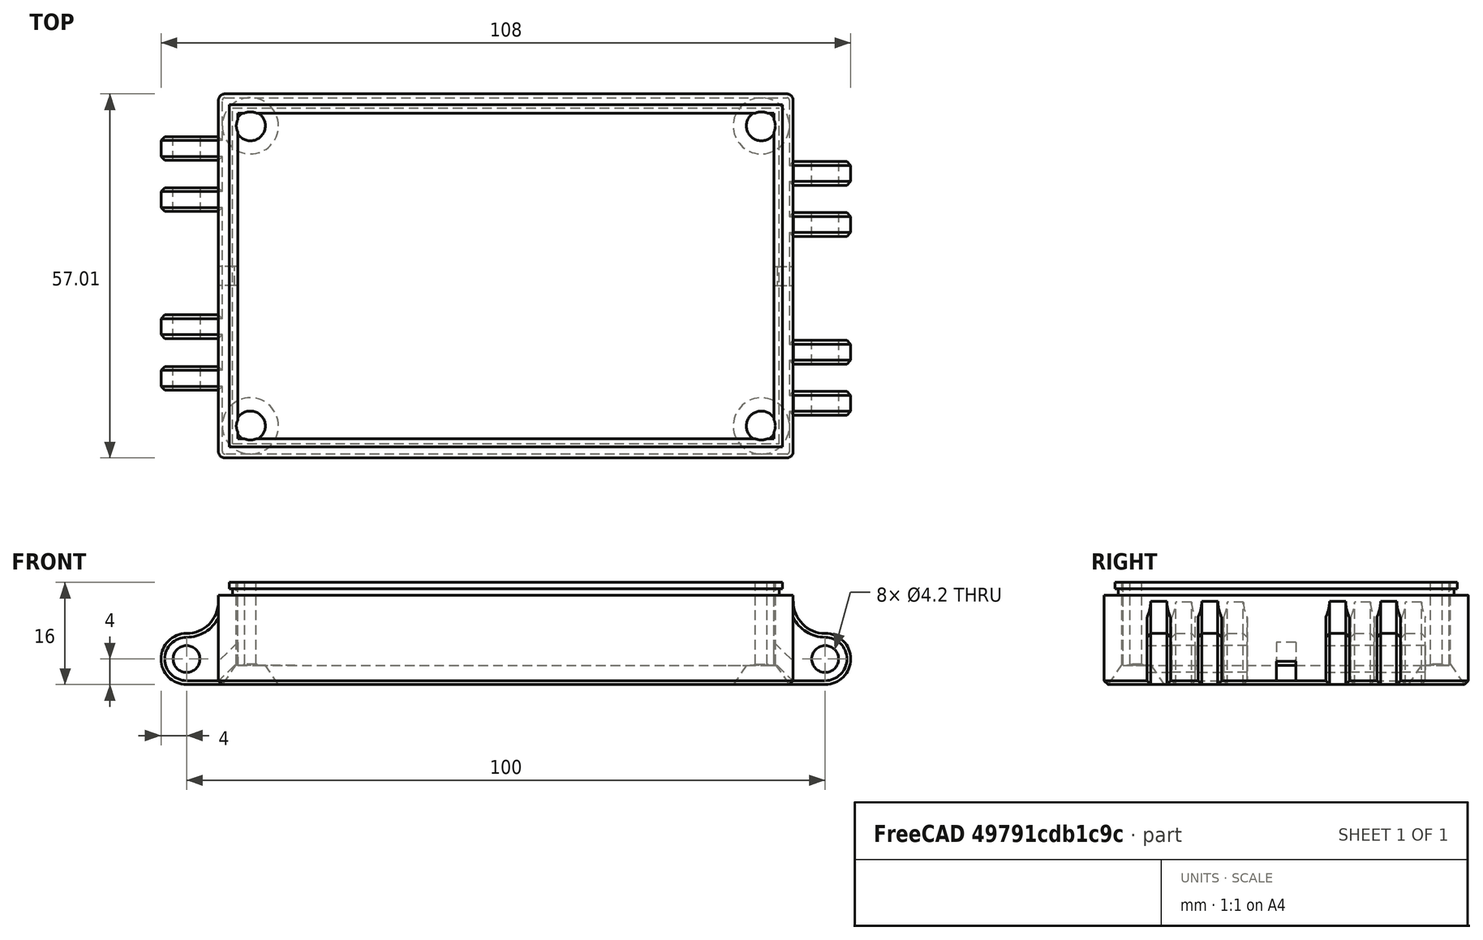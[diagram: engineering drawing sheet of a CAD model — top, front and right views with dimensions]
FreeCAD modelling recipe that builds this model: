
FCSTD DOCUMENT  (FreeCAD 0.16R)
Label: BoxBottom
License: All rights reserved
LicenseURL: http://en.wikipedia.org/wiki/All_rights_reserved
objects: Part::Chamfer×17, Part::Box×13, Part::MultiFuse×11, Sketcher::SketchObject×9, PartDesign::Pad×9, Part::Cut×5, Part::Cylinder×4, Part::Cone×4, Mesh::Feature×1
note: 81 computed .brp shape members not serialized (recipe doc carries the construction recipe); baked Part::Feature solids carry a one-line shape summary decoded from their .brp

FEATURE [Sketcher::SketchObject] Sketch002
  sketch-geometry (8):
    g0: LineSegment StartX=16.0115 StartY=-28 StartZ=0 EndX=-72 EndY=-28 EndZ=0
    g1: LineSegment StartX=-73.0008 StartY=-26.9992 StartZ=0 EndX=-73.0008 EndY=28.0015 EndZ=0
    g2: LineSegment StartX=-71.9972 StartY=29.005 StartZ=0 EndX=15.9984 EndY=29.005 EndZ=0
    g3: LineSegment StartX=16.9833 StartY=28.0201 StartZ=0 EndX=16.9833 EndY=-27.0282 EndZ=0
    g4: ArcOfCircle CenterX=16.0115 CenterY=-27.0282 CenterZ=0 NormalX=0 NormalY=0 NormalZ=1 Radius=0.97176 StartAngle=4.71239 EndAngle=6.28319
    g5: ArcOfCircle CenterX=-72 CenterY=-26.9992 CenterZ=0 NormalX=0 NormalY=0 NormalZ=1 Radius=1.00077 StartAngle=3.14159 EndAngle=4.71239
    g6: ArcOfCircle CenterX=-71.9972 CenterY=28.0015 CenterZ=0 NormalX=0 NormalY=0 NormalZ=1 Radius=1.00354 StartAngle=1.5708 EndAngle=3.14159
    g7: ArcOfCircle CenterX=15.9984 CenterY=28.0201 CenterZ=0 NormalX=0 NormalY=0 NormalZ=1 Radius=0.984903 StartAngle=0 EndAngle=1.5708
  constraints (12):
    c: Horizontal(g0)
    c: Horizontal(g2)
    c: Vertical(g1)
    c: Vertical(g3)
    c: Tangent(g3,g4) = 1.5708
    c: Tangent(g0,g4) = 1.5708
    c: Tangent(g1,g5) = 1.5708
    c: Tangent(g0,g5) = 1.5708
    c: Tangent(g1,g6) = 1.5708
    c: Tangent(g2,g6) = 1.5708
    c: Tangent(g2,g7) = 1.5708
    c: Tangent(g3,g7) = 1.5708
FEATURE [PartDesign::Pad] Pad013
  Length = 16
  Length2 = 100
  Sketch = -> Sketch002
  Type = 0
FEATURE [Part::Box] Box010  label="Würfel010"
  Height = 25
  Length = 84
  Placement = pos=(-70,-25,3) rot=(0,0,1;0rad)
  Width = 51
FEATURE [Part::Cut] Cut011
  Base = -> Pad013
  Tool = -> Box010
FEATURE [Part::Box] Box  label="Rand002"
  Height = 2
  Length = 90
  Placement = pos=(-73,27.3,14) rot=(0,0,1;0rad)
  Width = 2
FEATURE [Part::Box] Box011  label="Rand001"
  Height = 2
  Length = 90
  Placement = pos=(-73,-28.3,14) rot=(0,0,1;0rad)
  Width = 2
FEATURE [Part::Box] Box012  label="Rand003"
  Height = 2
  Length = 2
  Placement = pos=(-73.3,-28,14) rot=(0,0,1;0rad)
  Width = 57
FEATURE [Part::Box] Box013  label="Rand004"
  Height = 2
  Length = 2
  Placement = pos=(15.3,-28,14) rot=(0,0,1;0rad)
  Width = 57
FEATURE [Part::MultiFuse] Fusion  label="RandFraesung"
  Shapes = -> [Box013,Box012,Box011,Box]
FEATURE [Part::Cut] Cut
  Base = -> Cut011
  Tool = -> Fusion
FEATURE [Part::Box] Box014  label="Rand005"
  Height = 1
  Length = 90
  Placement = pos=(-74,26.8,14) rot=(0,0,1;0rad)
  Width = 1
FEATURE [Part::Box] Box015  label="Rand006"
  Height = 1
  Length = 90
  Placement = pos=(-74,-26.8,14) rot=(0,0,1;0rad)
  Width = 1
FEATURE [Part::Box] Box016  label="Rand007"
  Height = 1
  Length = 1
  Placement = pos=(-71.8,-28,14) rot=(0,0,1;0rad)
  Width = 57
FEATURE [Part::Box] Box017  label="Rand008"
  Height = 1
  Length = 1
  Placement = pos=(14.8,-28,14) rot=(0,0,1;0rad)
  Width = 57
FEATURE [Part::MultiFuse] Fusion001  label="NutFraesung"
  Shapes = -> [Box017,Box014,Box015,Box016]
FEATURE [Part::Cut] Cut012
  Base = -> Cut
  Tool = -> Fusion001
FEATURE [Part::Chamfer] Chamfer
  Base = -> Cut012
  Edges = 1 edges r=0.6: [Edge1]
FEATURE [Part::Box] Box018  label="Kabeltunnel"
  Height = 2.2
  Length = 10
  Placement = pos=(12,-1,5.5) rot=(0,1,0;0.785398rad)
  Width = 3
FEATURE [Sketcher::SketchObject] MirroredSketch004
  Placement = pos=(0,0,0) rot=(1,0,0;1.5708rad)
  sketch-geometry (7):
    g0: ArcOfCircle CenterX=0 CenterY=0 CenterZ=0 NormalX=0 NormalY=0 NormalZ=1 Radius=4 StartAngle=4.71239 EndAngle=7.85398
    g1: Circle CenterX=0 CenterY=0 CenterZ=0 NormalX=0 NormalY=0 NormalZ=1 Radius=2.1
    g2: LineSegment StartX=-6 StartY=9 StartZ=0 EndX=-6 EndY=-4 EndZ=0
    g3: LineSegment StartX=-6 StartY=-4 StartZ=0 EndX=0 EndY=-4 EndZ=0
    g4: LineSegment StartX=-5.47498 StartY=9 StartZ=0 EndX=-5 EndY=9 EndZ=0
    g5: ArcOfCircle CenterX=0 CenterY=9 CenterZ=0 NormalX=0 NormalY=0 NormalZ=1 Radius=5 StartAngle=3.14159 EndAngle=4.71239
    g6: LineSegment StartX=-6 StartY=9 StartZ=0 EndX=-5.47498 EndY=9 EndZ=0
  constraints (7):
    c: Coincident(g2,g3)
    c: Horizontal(g3)
    c: Vertical(g2)
    c: Coincident(g0,g3)
    c: Coincident(g5,g0)
    c: Coincident(g6,g4)
    c: Horizontal(g6)
FEATURE [PartDesign::Pad] Pad017  label="Lasche2Rechts004"
  Length = 3.7
  Length2 = 100
  Placement = pos=(0,0,0) rot=(1,0,0;1.5708rad)
  Sketch = -> MirroredSketch004
  Type = 0
FEATURE [Part::Chamfer] Chamfer009
  Base = -> Pad017
  Edges = 3 edges r=0.6: [Edge7,Edge10,Edge13]
FEATURE [Part::Chamfer] Chamfer010  label="Lasche2Rechts005"
  Base = -> Chamfer009
  Edges = 3 edges r=0.6: [Edge7,Edge11,Edge12]
  Placement = pos=(22,-17.6,4) rot=(0,0,1;0rad)
FEATURE [Sketcher::SketchObject] MirroredSketch005
  Placement = pos=(0,0,0) rot=(1,0,0;1.5708rad)
  sketch-geometry (7):
    g0: ArcOfCircle CenterX=0 CenterY=0 CenterZ=0 NormalX=0 NormalY=0 NormalZ=1 Radius=4 StartAngle=4.71239 EndAngle=7.85398
    g1: Circle CenterX=0 CenterY=0 CenterZ=0 NormalX=0 NormalY=0 NormalZ=1 Radius=2.1
    g2: LineSegment StartX=-6 StartY=9 StartZ=0 EndX=-6 EndY=-4 EndZ=0
    g3: LineSegment StartX=-6 StartY=-4 StartZ=0 EndX=0 EndY=-4 EndZ=0
    g4: LineSegment StartX=-5.47498 StartY=9 StartZ=0 EndX=-5 EndY=9 EndZ=0
    g5: ArcOfCircle CenterX=0 CenterY=9 CenterZ=0 NormalX=0 NormalY=0 NormalZ=1 Radius=5 StartAngle=3.14159 EndAngle=4.71239
    g6: LineSegment StartX=-6 StartY=9 StartZ=0 EndX=-5.47498 EndY=9 EndZ=0
  constraints (7):
    c: Coincident(g2,g3)
    c: Horizontal(g3)
    c: Vertical(g2)
    c: Coincident(g0,g3)
    c: Coincident(g5,g0)
    c: Coincident(g6,g4)
    c: Horizontal(g6)
FEATURE [PartDesign::Pad] Pad018  label="Lasche2Rechts006"
  Length = 3.7
  Length2 = 100
  Placement = pos=(0,0,0) rot=(1,0,0;1.5708rad)
  Sketch = -> MirroredSketch005
  Type = 0
FEATURE [Part::Chamfer] Chamfer011
  Base = -> Pad018
  Edges = 3 edges r=0.6: [Edge7,Edge10,Edge13]
FEATURE [Part::Chamfer] Chamfer012  label="Lasche2Rechts007"
  Base = -> Chamfer011
  Edges = 3 edges r=0.6: [Edge7,Edge11,Edge12]
  Placement = pos=(22,-9.6,4) rot=(0,0,1;0rad)
FEATURE [Sketcher::SketchObject] MirroredSketch006
  Placement = pos=(0,0,0) rot=(1,0,0;1.5708rad)
  sketch-geometry (7):
    g0: ArcOfCircle CenterX=0 CenterY=0 CenterZ=0 NormalX=0 NormalY=0 NormalZ=1 Radius=4 StartAngle=4.71239 EndAngle=7.85398
    g1: Circle CenterX=0 CenterY=0 CenterZ=0 NormalX=0 NormalY=0 NormalZ=1 Radius=2.1
    g2: LineSegment StartX=-6 StartY=9 StartZ=0 EndX=-6 EndY=-4 EndZ=0
    g3: LineSegment StartX=-6 StartY=-4 StartZ=0 EndX=0 EndY=-4 EndZ=0
    g4: LineSegment StartX=-5.47498 StartY=9 StartZ=0 EndX=-5 EndY=9 EndZ=0
    g5: ArcOfCircle CenterX=0 CenterY=9 CenterZ=0 NormalX=0 NormalY=0 NormalZ=1 Radius=5 StartAngle=3.14159 EndAngle=4.71239
    g6: LineSegment StartX=-6 StartY=9 StartZ=0 EndX=-5.47498 EndY=9 EndZ=0
  constraints (7):
    c: Coincident(g2,g3)
    c: Horizontal(g3)
    c: Vertical(g2)
    c: Coincident(g0,g3)
    c: Coincident(g5,g0)
    c: Coincident(g6,g4)
    c: Horizontal(g6)
FEATURE [PartDesign::Pad] Pad019  label="Lasche2Rechts008"
  Length = 3.7
  Length2 = 100
  Placement = pos=(0,0,0) rot=(1,0,0;1.5708rad)
  Sketch = -> MirroredSketch006
  Type = 0
FEATURE [Part::Chamfer] Chamfer013
  Base = -> Pad019
  Edges = 3 edges r=0.6: [Edge7,Edge10,Edge13]
FEATURE [Part::Chamfer] Chamfer014  label="Lasche2Rechts009"
  Base = -> Chamfer013
  Edges = 3 edges r=0.6: [Edge7,Edge11,Edge12]
  Placement = pos=(22,10.4,4) rot=(0,0,1;0rad)
FEATURE [Sketcher::SketchObject] MirroredSketch007
  Placement = pos=(0,0,0) rot=(1,0,0;1.5708rad)
  sketch-geometry (7):
    g0: ArcOfCircle CenterX=0 CenterY=0 CenterZ=0 NormalX=0 NormalY=0 NormalZ=1 Radius=4 StartAngle=4.71239 EndAngle=7.85398
    g1: Circle CenterX=0 CenterY=0 CenterZ=0 NormalX=0 NormalY=0 NormalZ=1 Radius=2.1
    g2: LineSegment StartX=-6 StartY=9 StartZ=0 EndX=-6 EndY=-4 EndZ=0
    g3: LineSegment StartX=-6 StartY=-4 StartZ=0 EndX=0 EndY=-4 EndZ=0
    g4: LineSegment StartX=-5.47498 StartY=9 StartZ=0 EndX=-5 EndY=9 EndZ=0
    g5: ArcOfCircle CenterX=0 CenterY=9 CenterZ=0 NormalX=0 NormalY=0 NormalZ=1 Radius=5 StartAngle=3.14159 EndAngle=4.71239
    g6: LineSegment StartX=-6 StartY=9 StartZ=0 EndX=-5.47498 EndY=9 EndZ=0
  constraints (7):
    c: Coincident(g2,g3)
    c: Horizontal(g3)
    c: Vertical(g2)
    c: Coincident(g0,g3)
    c: Coincident(g5,g0)
    c: Coincident(g6,g4)
    c: Horizontal(g6)
FEATURE [PartDesign::Pad] Pad020  label="Lasche2Rechts010"
  Length = 3.7
  Length2 = 100
  Placement = pos=(0,0,0) rot=(1,0,0;1.5708rad)
  Sketch = -> MirroredSketch007
  Type = 0
FEATURE [Part::Chamfer] Chamfer015
  Base = -> Pad020
  Edges = 3 edges r=0.6: [Edge7,Edge10,Edge13]
FEATURE [Part::Chamfer] Chamfer016  label="Lasche2Rechts011"
  Base = -> Chamfer015
  Edges = 3 edges r=0.6: [Edge7,Edge11,Edge12]
  Placement = pos=(22,18.4,4) rot=(0,0,1;0rad)
FEATURE [Part::Cylinder] Cylinder005  label="Zylinder"
  Angle = 360
  Height = 16
  Placement = pos=(12,-23,-1) rot=(0,0,1;0rad)
  Radius = 2.2
FEATURE [Part::Cone] Cone  label="Kegel"
  Angle = 360
  Height = 3.2
  Placement = pos=(12,-23,-1) rot=(0,0,1;0rad)
  Radius1 = 4.4
  Radius2 = 2.2
FEATURE [Part::MultiFuse] Fusion002  label="Bohrung001"
  Placement = pos=(0,0,1) rot=(0,0,1;0rad)
  Shapes = -> [Cylinder005,Cone]
FEATURE [Part::Cylinder] Cylinder006  label="Zylinder003"
  Angle = 360
  Height = 16
  Placement = pos=(12,-23,-1) rot=(0,0,1;0rad)
  Radius = 2.2
FEATURE [Part::Cone] Cone001  label="Kegel001"
  Angle = 360
  Height = 3.2
  Placement = pos=(12,-23,-1) rot=(0,0,1;0rad)
  Radius1 = 4.4
  Radius2 = 2.2
FEATURE [Part::MultiFuse] Fusion003  label="Bohrung002"
  Placement = pos=(0,47,1) rot=(0,0,1;0rad)
  Shapes = -> [Cylinder006,Cone001]
FEATURE [Part::Cylinder] Cylinder007  label="Zylinder004"
  Angle = 360
  Height = 16
  Placement = pos=(12,-23,-1) rot=(0,0,1;0rad)
  Radius = 2.2
FEATURE [Part::Cone] Cone002  label="Kegel002"
  Angle = 360
  Height = 3.2
  Placement = pos=(12,-23,-1) rot=(0,0,1;0rad)
  Radius1 = 4.4
  Radius2 = 2.2
FEATURE [Part::MultiFuse] Fusion004  label="Bohrung003"
  Placement = pos=(-80,0,1) rot=(0,0,1;0rad)
  Shapes = -> [Cylinder007,Cone002]
FEATURE [Part::Cylinder] Cylinder008  label="Zylinder005"
  Angle = 360
  Height = 16
  Placement = pos=(12,-23,-1) rot=(0,0,1;0rad)
  Radius = 2.2
FEATURE [Part::Cone] Cone003  label="Kegel003"
  Angle = 360
  Height = 3.2
  Placement = pos=(12,-23,-1) rot=(0,0,1;0rad)
  Radius1 = 4.4
  Radius2 = 2.2
FEATURE [Part::MultiFuse] Fusion005  label="Bohrung004"
  Placement = pos=(-80,47,1) rot=(0,0,1;0rad)
  Shapes = -> [Cylinder008,Cone003]
FEATURE [Part::MultiFuse] Fusion006  label="Bohrungen"
  Shapes = -> [Fusion003,Fusion002,Fusion004,Fusion005]
FEATURE [Part::Box] Box019  label="KabelTunnelGlatt"
  Height = 1
  Length = 10
  Placement = pos=(5,-1,3) rot=(0,0,1;0rad)
  Width = 3
FEATURE [Part::MultiFuse] Fusion007  label="Tunnel1"
  Shapes = -> [Box018,Box019]
FEATURE [Part::Box] Box020  label="Kabeltunnel001"
  Height = 2.2
  Length = 10
  Placement = pos=(12,-1,5.5) rot=(0,1,0;0.785398rad)
  Width = 3
FEATURE [Part::Box] Box021  label="KabelTunnelGlatt001"
  Height = 1
  Length = 10
  Placement = pos=(5,-1,3) rot=(0,0,1;0rad)
  Width = 3
FEATURE [Part::MultiFuse] Fusion008  label="Tunnel2"
  Placement = pos=(-56,1,0) rot=(0,0,1;3.14159rad)
  Shapes = -> [Box020,Box021]
FEATURE [Part::MultiFuse] Fusion009
  Shapes = -> [Fusion008,Fusion007]
FEATURE [Part::Cut] Cut013
  Base = -> Chamfer
  Tool = -> Fusion009
FEATURE [Sketcher::SketchObject] MirroredSketch008
  Placement = pos=(0,0,0) rot=(1,0,0;1.5708rad)
  sketch-geometry (7):
    g0: ArcOfCircle CenterX=0 CenterY=0 CenterZ=0 NormalX=0 NormalY=0 NormalZ=1 Radius=4 StartAngle=4.71239 EndAngle=7.85398
    g1: Circle CenterX=0 CenterY=0 CenterZ=0 NormalX=0 NormalY=0 NormalZ=1 Radius=2.1
    g2: LineSegment StartX=-6 StartY=9 StartZ=0 EndX=-6 EndY=-4 EndZ=0
    g3: LineSegment StartX=-6 StartY=-4 StartZ=0 EndX=0 EndY=-4 EndZ=0
    g4: LineSegment StartX=-5.47498 StartY=9 StartZ=0 EndX=-5 EndY=9 EndZ=0
    g5: ArcOfCircle CenterX=0 CenterY=9 CenterZ=0 NormalX=0 NormalY=0 NormalZ=1 Radius=5 StartAngle=3.14159 EndAngle=4.71239
    g6: LineSegment StartX=-6 StartY=9 StartZ=0 EndX=-5.47498 EndY=9 EndZ=0
  constraints (7):
    c: Coincident(g2,g3)
    c: Horizontal(g3)
    c: Vertical(g2)
    c: Coincident(g0,g3)
    c: Coincident(g5,g0)
    c: Coincident(g6,g4)
    c: Horizontal(g6)
FEATURE [PartDesign::Pad] Pad021  label="Lasche2Rechts012"
  Length = 3.7
  Length2 = 100
  Placement = pos=(0,0,0) rot=(1,0,0;1.5708rad)
  Sketch = -> MirroredSketch008
  Type = 0
FEATURE [Part::Chamfer] Chamfer017
  Base = -> Pad021
  Edges = 3 edges r=0.6: [Edge7,Edge10,Edge13]
FEATURE [Part::Chamfer] Chamfer018  label="Lasche2Rechts013"
  Base = -> Chamfer017
  Edges = 3 edges r=0.6: [Edge7,Edge11,Edge12]
  Placement = pos=(-78,18.6,4) rot=(0,0,1;3.14159rad)
FEATURE [Sketcher::SketchObject] MirroredSketch009
  Placement = pos=(0,0,0) rot=(1,0,0;1.5708rad)
  sketch-geometry (7):
    g0: ArcOfCircle CenterX=0 CenterY=0 CenterZ=0 NormalX=0 NormalY=0 NormalZ=1 Radius=4 StartAngle=4.71239 EndAngle=7.85398
    g1: Circle CenterX=0 CenterY=0 CenterZ=0 NormalX=0 NormalY=0 NormalZ=1 Radius=2.1
    g2: LineSegment StartX=-6 StartY=9 StartZ=0 EndX=-6 EndY=-4 EndZ=0
    g3: LineSegment StartX=-6 StartY=-4 StartZ=0 EndX=0 EndY=-4 EndZ=0
    g4: LineSegment StartX=-5.47498 StartY=9 StartZ=0 EndX=-5 EndY=9 EndZ=0
    g5: ArcOfCircle CenterX=0 CenterY=9 CenterZ=0 NormalX=0 NormalY=0 NormalZ=1 Radius=5 StartAngle=3.14159 EndAngle=4.71239
    g6: LineSegment StartX=-6 StartY=9 StartZ=0 EndX=-5.47498 EndY=9 EndZ=0
  constraints (7):
    c: Coincident(g2,g3)
    c: Horizontal(g3)
    c: Vertical(g2)
    c: Coincident(g0,g3)
    c: Coincident(g5,g0)
    c: Coincident(g6,g4)
    c: Horizontal(g6)
FEATURE [PartDesign::Pad] Pad022  label="Lasche2Rechts014"
  Length = 3.7
  Length2 = 100
  Placement = pos=(0,0,0) rot=(1,0,0;1.5708rad)
  Sketch = -> MirroredSketch009
  Type = 0
FEATURE [Part::Chamfer] Chamfer019
  Base = -> Pad022
  Edges = 3 edges r=0.6: [Edge7,Edge10,Edge13]
FEATURE [Part::Chamfer] Chamfer020  label="Lasche2Rechts015"
  Base = -> Chamfer019
  Edges = 3 edges r=0.6: [Edge7,Edge11,Edge12]
  Placement = pos=(-78,10.6,4) rot=(0,0,1;3.14159rad)
FEATURE [Sketcher::SketchObject] MirroredSketch010
  Placement = pos=(0,0,0) rot=(1,0,0;1.5708rad)
  sketch-geometry (7):
    g0: ArcOfCircle CenterX=0 CenterY=0 CenterZ=0 NormalX=0 NormalY=0 NormalZ=1 Radius=4 StartAngle=4.71239 EndAngle=7.85398
    g1: Circle CenterX=0 CenterY=0 CenterZ=0 NormalX=0 NormalY=0 NormalZ=1 Radius=2.1
    g2: LineSegment StartX=-6 StartY=9 StartZ=0 EndX=-6 EndY=-4 EndZ=0
    g3: LineSegment StartX=-6 StartY=-4 StartZ=0 EndX=0 EndY=-4 EndZ=0
    g4: LineSegment StartX=-5.47498 StartY=9 StartZ=0 EndX=-5 EndY=9 EndZ=0
    g5: ArcOfCircle CenterX=0 CenterY=9 CenterZ=0 NormalX=0 NormalY=0 NormalZ=1 Radius=5 StartAngle=3.14159 EndAngle=4.71239
    g6: LineSegment StartX=-6 StartY=9 StartZ=0 EndX=-5.47498 EndY=9 EndZ=0
  constraints (7):
    c: Coincident(g2,g3)
    c: Horizontal(g3)
    c: Vertical(g2)
    c: Coincident(g0,g3)
    c: Coincident(g5,g0)
    c: Coincident(g6,g4)
    c: Horizontal(g6)
FEATURE [PartDesign::Pad] Pad023  label="Lasche2Rechts016"
  Length = 3.7
  Length2 = 100
  Placement = pos=(0,0,0) rot=(1,0,0;1.5708rad)
  Sketch = -> MirroredSketch010
  Type = 0
FEATURE [Part::Chamfer] Chamfer021
  Base = -> Pad023
  Edges = 3 edges r=0.6: [Edge7,Edge10,Edge13]
FEATURE [Part::Chamfer] Chamfer022  label="Lasche2Rechts017"
  Base = -> Chamfer021
  Edges = 3 edges r=0.6: [Edge7,Edge11,Edge12]
  Placement = pos=(-78,-9.3,4) rot=(0,0,1;3.14159rad)
FEATURE [Sketcher::SketchObject] MirroredSketch011
  Placement = pos=(0,0,0) rot=(1,0,0;1.5708rad)
  sketch-geometry (7):
    g0: ArcOfCircle CenterX=0 CenterY=0 CenterZ=0 NormalX=0 NormalY=0 NormalZ=1 Radius=4 StartAngle=4.71239 EndAngle=7.85398
    g1: Circle CenterX=0 CenterY=0 CenterZ=0 NormalX=0 NormalY=0 NormalZ=1 Radius=2.1
    g2: LineSegment StartX=-6 StartY=9 StartZ=0 EndX=-6 EndY=-4 EndZ=0
    g3: LineSegment StartX=-6 StartY=-4 StartZ=0 EndX=0 EndY=-4 EndZ=0
    g4: LineSegment StartX=-5.47498 StartY=9 StartZ=0 EndX=-5 EndY=9 EndZ=0
    g5: ArcOfCircle CenterX=0 CenterY=9 CenterZ=0 NormalX=0 NormalY=0 NormalZ=1 Radius=5 StartAngle=3.14159 EndAngle=4.71239
    g6: LineSegment StartX=-6 StartY=9 StartZ=0 EndX=-5.47498 EndY=9 EndZ=0
  constraints (7):
    c: Coincident(g2,g3)
    c: Horizontal(g3)
    c: Vertical(g2)
    c: Coincident(g0,g3)
    c: Coincident(g5,g0)
    c: Coincident(g6,g4)
    c: Horizontal(g6)
FEATURE [PartDesign::Pad] Pad024  label="Lasche2Rechts018"
  Length = 3.7
  Length2 = 100
  Placement = pos=(0,0,0) rot=(1,0,0;1.5708rad)
  Sketch = -> MirroredSketch011
  Type = 0
FEATURE [Part::Chamfer] Chamfer023
  Base = -> Pad024
  Edges = 3 edges r=0.6: [Edge7,Edge10,Edge13]
FEATURE [Part::Chamfer] Chamfer024  label="Lasche2Rechts019"
  Base = -> Chamfer023
  Edges = 3 edges r=0.6: [Edge7,Edge11,Edge12]
  Placement = pos=(-78,-17.4,4) rot=(0,0,1;3.14159rad)
FEATURE [Part::MultiFuse] Fusion010
  Shapes = -> [Chamfer024,Chamfer012,Chamfer010,Chamfer018,Chamfer014,Chamfer016,Cut013,Chamfer022,Chamfer020]
FEATURE [Part::Cut] Cut014
  Base = -> Fusion010
  Tool = -> Fusion006
FEATURE [Mesh::Feature] Mesh  label="Cut014 (Meshed)"
